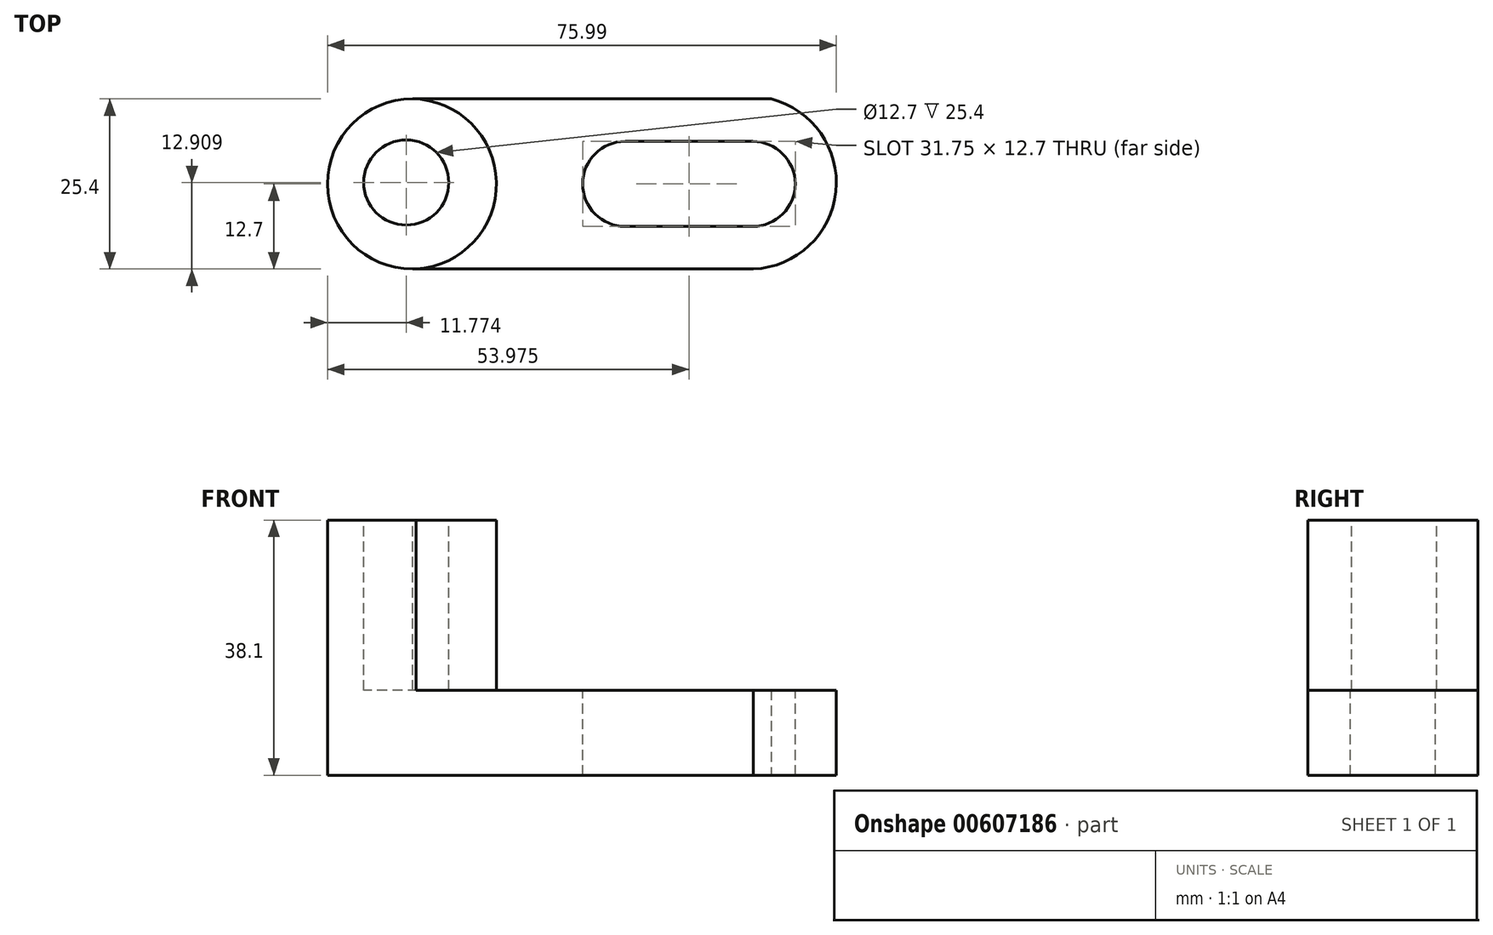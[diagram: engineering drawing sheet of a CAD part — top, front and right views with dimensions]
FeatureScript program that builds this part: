
annotation { "Feature Type Name" : "Feature", "Feature Type Description" : "" }
export const myFeature = defineFeature(function(context is Context, id is Id, definition is map)
    precondition{}
    {
        {
            var Q0;
            Q0=qCreatedBy(makeId("Front.planeOp"),FACE);
            var sketch = newSketch(context, id + "F0", { "sketchPlane" : qUnion([Q0])});
            skLineSegment(sketch, "E0", {"start": v(0, 38.1) * mm, "end": v(0, 0) * mm});
            skLineSegment(sketch, "E1", {"start": v(0, 0) * mm, "end": v(76.2, 0) * mm});
            skLineSegment(sketch, "E2", {"start": v(76.2, 0) * mm, "end": v(76.2, 12.7) * mm});
            skLineSegment(sketch, "E3", {"start": v(76.2, 12.7) * mm, "end": v(25.4, 12.7) * mm});
            skLineSegment(sketch, "E4", {"start": v(25.4, 12.7) * mm, "end": v(25.4, 38.1) * mm});
            skLineSegment(sketch, "E5", {"start": v(25.4, 38.1) * mm, "end": v(0, 38.1) * mm});
            skSolve(sketch);
        }
        {
            var Q0;
            Q0=makeQuery(id+"F0.imprint","IMPRINT",FACE,{"disambiguationData":[TD([[makeQuery(id+"F0.imprint","IMPRINT",EDGE,{"derivedFrom":sQuery(id+"F0.wireOp",EDGE,"E0")}),1.0]])]});
            extrude(context, id + "F1", {"entities" : qUnion([Q0]), "oppositeDirection" : true, "depth" : 25.4 * mm, "offsetDistance" : 25.4 * mm});
        }
        {
            var Q0;
            Q0=makeQuery(id+"F1.opExtrude","SWEPT_FACE",FACE,{"disambiguationData":[OSD([sQuery(id+"F0.wireOp",EDGE,"E3")])]});
            var sketch = newSketch(context, id + "F2", { "sketchPlane" : qUnion([Q0])});
            skPoint(sketch, "E6.centerSnap0", {"position": v(25.4, 12.7) * mm});
            skLineSegment(sketch, "E7", {"start": v(44.45, 19.05) * mm, "end": v(63.5, 19.05) * mm});
            skLineSegment(sketch, "E8", {"start": v(44.45, 6.35) * mm, "end": v(63.5, 6.35) * mm});
            skArc(sketch, "E9", {"start": v(63.5, 6.35) * mm, "mid": v(69.85, 12.7) * mm, "end": v(63.5, 19.05) * mm});
            skArc(sketch, "E10", {"start": v(44.45, 19.05) * mm, "mid": v(38.1, 12.7) * mm, "end": v(44.45, 6.35) * mm});
            skSolve(sketch);
        }
        {
            var Q0;
            Q0=makeQuery(id+"F2.imprint","IMPRINT",FACE,{"disambiguationData":[TD([[makeQuery(id+"F2.imprint","IMPRINT",EDGE,{"derivedFrom":sQuery(id+"F2.wireOp",EDGE,"E7")}),-1.0]])]});
            extrude(context, id + "F3", {"entities" : qUnion([Q0]), "operationType" : NewBodyOperationType.REMOVE, "oppositeDirection" : true, "depth" : 25.4 * mm, "offsetDistance" : 25.4 * mm});
        }
        {
            var Q0;
            Q0=makeQuery(id+"F1.opExtrude","SWEPT_FACE",FACE,{"disambiguationData":[OSD([sQuery(id+"F0.wireOp",EDGE,"E5")])]});
            var sketch = newSketch(context, id + "F4", { "sketchPlane" : qUnion([Q0])});
            skCircle(sketch, "E11", {"center": v(11.77, 12.9) * mm, "radius": 6.35 * mm});
            skArc(sketch, "E12", {"start": v(11.77, 0) * mm, "mid": v(25.22, 12.23) * mm, "end": v(12.7, 25.4) * mm});
            skSolve(sketch);
        }
        {
            var Q0;
            Q0=makeQuery(id+"F4.imprint","IMPRINT",FACE,{"disambiguationData":[TD([[makeQuery(id+"F4.imprint","IMPRINT",EDGE,{"derivedFrom":sQuery(id+"F4.wireOp",EDGE,"E11")}),1.0]])]});
            var Q1;
            {var subQ1=sQuery(id+"F0.wireOp",EDGE,"E5");var subQ6=makeQuery(id+"F1.opExtrude","SWEPT_EDGE",EDGE,{"disambiguationData":[OSD([sQuery(id+"F0.wireOp",EDGE,"E4"),subQ1])]});Q1=makeQuery(id+"F4.imprint","IMPRINT",FACE,{"disambiguationData":[TD([[makeQuery(id+"F4.imprint","IMPRINT",EDGE,{"derivedFrom":subQ6}),-1.0]])]});}
            extrude(context, id + "F5", {"entities" : qUnion([Q0, Q1]), "operationType" : NewBodyOperationType.REMOVE, "oppositeDirection" : true, "depth" : 25.4 * mm, "offsetDistance" : 25.4 * mm});
        }
        {
            var Q0;
            Q0=makeQuery(id+"F1.opExtrude","SWEPT_FACE",FACE,{"disambiguationData":[OSD([sQuery(id+"F0.wireOp",EDGE,"E5")])]});
            var sketch = newSketch(context, id + "F6", { "sketchPlane" : qUnion([Q0])});
            skArc(sketch, "E13", {"start": v(12.7, 25.4) * mm, "mid": v(0, 12.7) * mm, "end": v(12.7, 0) * mm});
            skSolve(sketch);
        }
        {
            var Q0;
            {var subQ1=sQuery(id+"F0.wireOp",EDGE,"E5");var subQ2=makeQuery(id+"F1.opExtrude","CAP_EDGE",EDGE,{"disambiguationData":[OSD([subQ1])],"isStart":false});Q0=makeQuery(id+"F6.imprint","IMPRINT",FACE,{"disambiguationData":[TD([[makeQuery(id+"F6.imprint","IMPRINT",EDGE,{"derivedFrom":subQ2}),1.0]])]});}
            var Q1;
            {var subQ0=sQuery(id+"F6.wireOp",EDGE,"E13");var subQ1=sQuery(id+"F0.wireOp",EDGE,"E5");var subQ2=makeQuery(id+"F1.opExtrude","CAP_EDGE",EDGE,{"disambiguationData":[OSD([subQ1])],"isStart":true});var subQ3=makeQuery(id+"F6.imprint","INTERSECT",VERTEX,{"derivedFrom":[subQ2,subQ0]});Q1=makeQuery(id+"F6.imprint","IMPRINT",FACE,{"disambiguationData":[TD([[makeQuery(id+"F6.imprint","IMPRINT",EDGE,{"disambiguationData":[TD([[subQ3,1.0]])],"derivedFrom":subQ0}),-1.0]])]});}
            extrude(context, id + "F7", {"entities" : qUnion([Q0, Q1]), "operationType" : NewBodyOperationType.REMOVE, "oppositeDirection" : true, "depth" : 25.4 * mm, "offsetDistance" : 25.4 * mm});
        }
        {
            var Q0;
            Q0=makeQuery(id+"F1.opExtrude","SWEPT_FACE",FACE,{"disambiguationData":[OSD([sQuery(id+"F0.wireOp",EDGE,"E1")])]});
            var sketch = newSketch(context, id + "F8", { "sketchPlane" : qUnion([Q0])});
            skArc(sketch, "E14", {"start": v(66.25, -25.4) * mm, "mid": v(75.85, -11.04) * mm, "end": v(62.56, 0) * mm});
            skSolve(sketch);
        }
        {
            var Q0;
            {var subQ1=sQuery(id+"F0.wireOp",EDGE,"E1");var subQ6=makeQuery(id+"F1.opExtrude","SWEPT_EDGE",EDGE,{"disambiguationData":[OSD([subQ1,sQuery(id+"F0.wireOp",EDGE,"E2")])]});Q0=makeQuery(id+"F8.imprint","IMPRINT",FACE,{"disambiguationData":[TD([[makeQuery(id+"F8.imprint","IMPRINT",EDGE,{"derivedFrom":subQ6}),1.0]])]});}
            extrude(context, id + "F9", {"entities" : qUnion([Q0]), "operationType" : NewBodyOperationType.REMOVE, "oppositeDirection" : true, "depth" : 25.4 * mm, "offsetDistance" : 25.4 * mm});
        }
        {
            var Q0;
            {var subQ0=sQuery(id+"F0.wireOp",EDGE,"E5");var subQ1=makeQuery(id+"F1.opExtrude","CAP_EDGE",EDGE,{"disambiguationData":[OSD([subQ0])],"isStart":true});var subQ2=sQuery(id+"F0.wireOp",EDGE,"E0");var subQ3=makeQuery(id+"F1.opExtrude","SWEPT_EDGE",EDGE,{"disambiguationData":[OSD([subQ2,subQ0])]});var subQ4=makeQuery(id+"F6.imprint","INTERSECT",VERTEX,{"derivedFrom":[subQ3,subQ1]});var subQ5=sQuery(id+"F6.wireOp",EDGE,"E13");var subQ6=makeQuery(id+"F6.imprint","INTERSECT",VERTEX,{"derivedFrom":[subQ1,subQ5]});Q0=makeQuery(id+"F7.boolean.opBoolean","COPY",FACE,{"derivedFrom":makeQuery(id+"F7.opExtrude","CAP_FACE",FACE,{"disambiguationData":[OSD([subQ2,subQ0,subQ5]),TDD([makeQuery(id+"F6.imprint","IMPRINT",EDGE,{"disambiguationData":[TD([[subQ6,1.0]])],"derivedFrom":subQ5}),makeQuery(id+"F6.imprint","IMPRINT",EDGE,{"disambiguationData":[TD([[subQ4,1.0]])],"derivedFrom":subQ3}),makeQuery(id+"F6.imprint","IMPRINT",EDGE,{"disambiguationData":[TD([[subQ6,-1.0]])],"derivedFrom":subQ1})])],"isStart":false})});}
            extrude(context, id + "F10", {"entities" : qUnion([Q0]), "operationType" : NewBodyOperationType.REMOVE, "oppositeDirection" : true, "depth" : 25.4 * mm, "offsetDistance" : 25.4 * mm});
        }
        {
            var Q0;
            {var subQ0=sQuery(id+"F0.wireOp",EDGE,"E5");var subQ1=makeQuery(id+"F1.opExtrude","CAP_EDGE",EDGE,{"disambiguationData":[OSD([subQ0])],"isStart":false});var subQ2=sQuery(id+"F0.wireOp",EDGE,"E0");var subQ3=makeQuery(id+"F1.opExtrude","SWEPT_EDGE",EDGE,{"disambiguationData":[OSD([subQ2,subQ0])]});var subQ4=sQuery(id+"F6.wireOp",EDGE,"E13");Q0=makeQuery(id+"F7.boolean.opBoolean","COPY",FACE,{"derivedFrom":makeQuery(id+"F7.opExtrude","CAP_FACE",FACE,{"disambiguationData":[OSD([subQ2,subQ0,subQ4]),TDD([makeQuery(id+"F6.imprint","IMPRINT",EDGE,{"disambiguationData":[TD([[makeQuery(id+"F6.imprint","INTERSECT",VERTEX,{"derivedFrom":[makeQuery(id+"F5.boolean.opBoolean","COPY",EDGE,{"derivedFrom":makeQuery(id+"F5.opExtrude","CAP_EDGE",EDGE,{"disambiguationData":[OSD([sQuery(id+"F4.wireOp",EDGE,"E12")])],"isStart":true})}),subQ1,subQ4]}),-1.0]])],"derivedFrom":subQ4}),makeQuery(id+"F6.imprint","IMPRINT",EDGE,{"derivedFrom":subQ1}),makeQuery(id+"F6.imprint","IMPRINT",EDGE,{"disambiguationData":[TD([[makeQuery(id+"F6.imprint","INTERSECT",VERTEX,{"derivedFrom":[subQ3,subQ1]}),-1.0]])],"derivedFrom":subQ3})])],"isStart":false})});}
            extrude(context, id + "F11", {"entities" : qUnion([Q0]), "operationType" : NewBodyOperationType.REMOVE, "oppositeDirection" : true, "depth" : 25.4 * mm, "offsetDistance" : 25.4 * mm});
        }
    });
